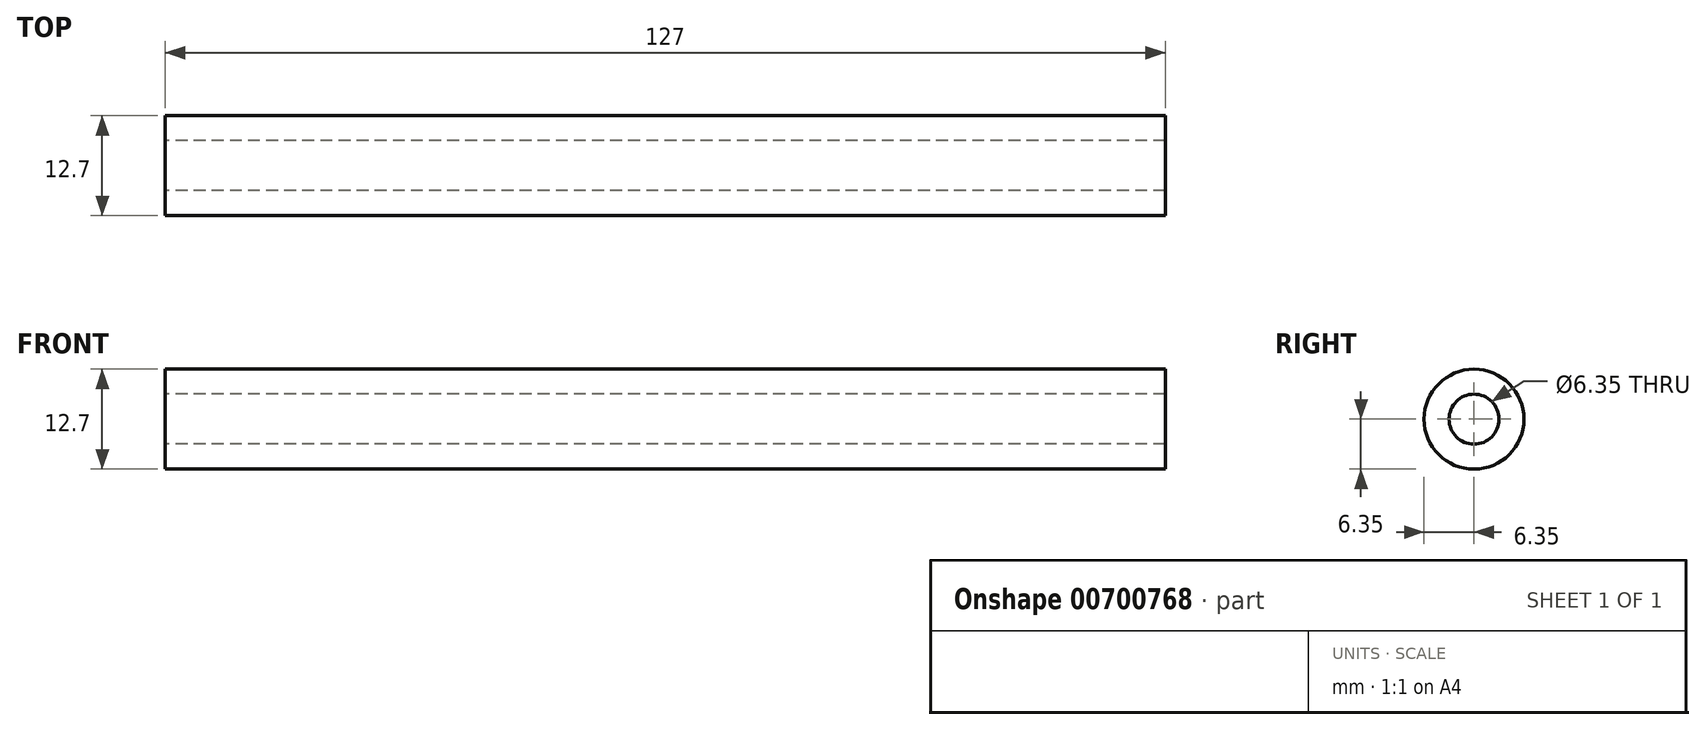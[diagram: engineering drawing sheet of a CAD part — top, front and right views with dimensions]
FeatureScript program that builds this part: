
annotation { "Feature Type Name" : "Feature", "Feature Type Description" : "" }
export const myFeature = defineFeature(function(context is Context, id is Id, definition is map)
    precondition{}
    {
        {
            var Q0;
            Q0=qCreatedBy(makeId("Right.planeOp"),FACE);
            var sketch = newSketch(context, id + "F0", { "sketchPlane" : qUnion([Q0])});
            skCircle(sketch, "E0", {"center": v(0, 0) * mm, "radius": 3.18 * mm});
            skCircle(sketch, "E1", {"center": v(0, 0) * mm, "radius": 6.35 * mm});
            skSolve(sketch);
        }
        {
            var Q0;
            Q0=makeQuery(id+"F0.imprint","IMPRINT",FACE,{"disambiguationData":[TD([[makeQuery(id+"F0.imprint","IMPRINT",EDGE,{"derivedFrom":sQuery(id+"F0.wireOp",EDGE,"E0")}),-1.0]])]});
            extrude(context, id + "F1", {"entities" : qUnion([Q0]), "endBound" : BoundingType.SYMMETRIC, "depth" : 127 * mm, "offsetDistance" : 25.4 * mm});
        }
    });
